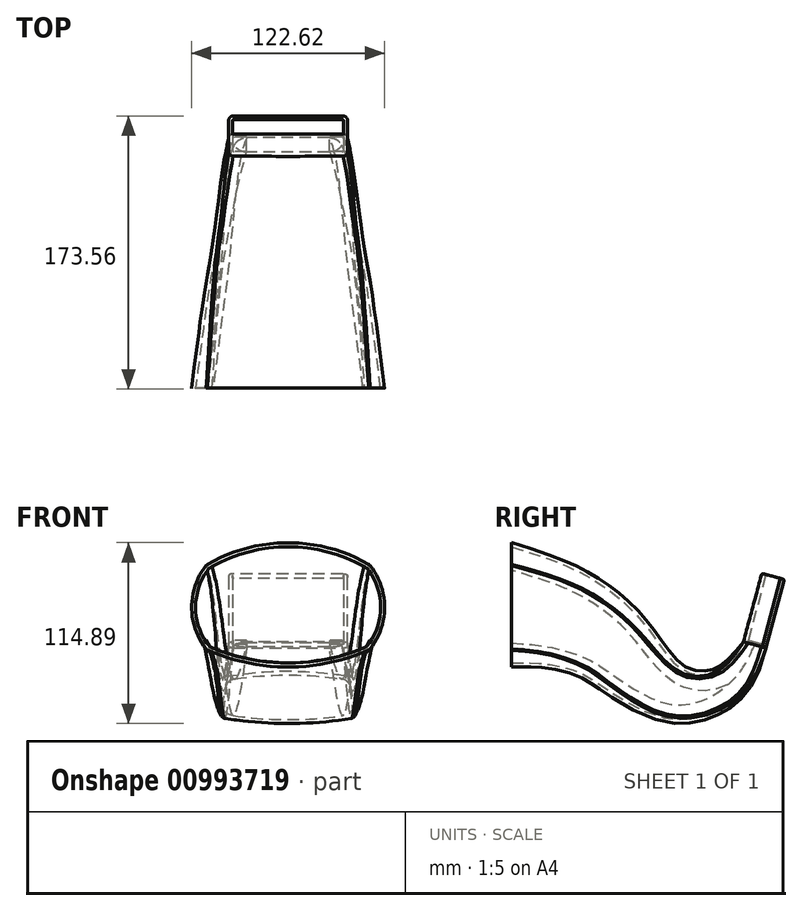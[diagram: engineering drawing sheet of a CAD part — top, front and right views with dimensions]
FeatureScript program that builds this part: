
annotation { "Feature Type Name" : "Feature", "Feature Type Description" : "" }
export const myFeature = defineFeature(function(context is Context, id is Id, definition is map)
    precondition{}
    {
        {
            var Q0;
            Q0=qCreatedBy(makeId("Right.planeOp"),FACE);
            var sketch = newSketch(context, id + "F0", { "sketchPlane" : qUnion([Q0])});
            skLineSegment(sketch, "E0", {"start": v(0, 0) * mm, "end": v(9.05, 33.77) * mm, "construction": true});
            skSolve(sketch);
        }
        {
            var Q0;
            Q0=sQuery(id+"F0.wireOp",EDGE,"E0");
            cPlane(context, id + "F1", {"entities" : qUnion([Q0]), "cplaneType" : CPlaneType.MID_PLANE, "offset" : 25 * mm, "width" : 150 * mm, "height" : 150 * mm});
        }
        {
            var Q0;
            Q0=qCreatedBy(id+"F1.planeOp",FACE);
            var sketch = newSketch(context, id + "F2", { "sketchPlane" : qUnion([Q0])});
            skLineSegment(sketch, "E1.bottom", {"start": v(35.25, 4.75) * mm, "end": v(-35.25, 4.75) * mm});
            skLineSegment(sketch, "E1.top", {"start": v(35.25, -4.75) * mm, "end": v(-35.25, -4.75) * mm});
            skLineSegment(sketch, "E1.left", {"start": v(35.25, 4.75) * mm, "end": v(35.25, -4.75) * mm});
            skLineSegment(sketch, "E1.right", {"start": v(-35.25, 4.75) * mm, "end": v(-35.25, -4.75) * mm});
            skLineSegment(sketch, "E2", {"start": v(35.25, 4.75) * mm, "end": v(-35.25, -4.75) * mm, "construction": true});
            skSolve(sketch);
        }
        {
            var Q0;
            Q0=qCreatedBy(makeId("Right.planeOp"),FACE);
            var sketch = newSketch(context, id + "F3", { "sketchPlane" : qUnion([Q0])});
            skPoint(sketch, "E3.0", {"position": v(4.52, 16.89) * mm});
            skFitSpline(sketch, "E4", {"points": [v(4.52, 16.89) * mm, v(-21.2, -13.25) * mm, v(-50.69, -13.25) * mm, v(-82.93, 11.56) * mm, v(-109.4, 29.2) * mm, v(-150, 40.77) * mm], "startDerivative": vector(-59.2, -227.9) * mm, "endDerivative": vector(-84.83, -3.64) * mm});
            skSolve(sketch);
        }
        {
            var Q0;
            Q0=qCreatedBy(makeId("Front.planeOp"),FACE);
            cPlane(context, id + "F4", {"entities" : qUnion([Q0]), "cplaneType" : CPlaneType.OFFSET, "offset" : 150 * mm, "width" : 150 * mm, "height" : 150 * mm});
        }
        {
            var Q0;
            Q0=qCreatedBy(id+"F4.planeOp",FACE);
            var sketch = newSketch(context, id + "F5", { "sketchPlane" : qUnion([Q0])});
            skLineSegment(sketch, "E5.bottom", {"start": v(-50, 65.77) * mm, "end": v(50, 65.77) * mm, "construction": true});
            skLineSegment(sketch, "E5.top", {"start": v(-50, 15.77) * mm, "end": v(50, 15.77) * mm, "construction": true});
            skLineSegment(sketch, "E5.left", {"start": v(-50, 65.77) * mm, "end": v(-50, 15.77) * mm, "construction": true});
            skLineSegment(sketch, "E5.right", {"start": v(50, 65.77) * mm, "end": v(50, 15.77) * mm, "construction": true});
            skLineSegment(sketch, "E6", {"start": v(-50, 65.77) * mm, "end": v(50, 15.77) * mm, "construction": true});
            skArc(sketch, "E7", {"start": v(50, 65.77) * mm, "mid": v(0, 79.17) * mm, "end": v(-50, 65.77) * mm});
            skArc(sketch, "E8", {"start": v(50, 15.77) * mm, "mid": v(58.78, 40.77) * mm, "end": v(50, 65.77) * mm});
            skArc(sketch, "E9", {"start": v(-50, 65.77) * mm, "mid": v(-58.78, 40.77) * mm, "end": v(-50, 15.77) * mm});
            skArc(sketch, "E10", {"start": v(-50, 15.77) * mm, "mid": v(0, 5.33) * mm, "end": v(50, 15.77) * mm});
            skSolve(sketch);
        }
        {
            var Q0;
            Q0=sQuery(id+"F3.wireOp",EDGE,"E4");
            var Q1;
            Q1=makeQuery(id+"F2.imprint","IMPRINT",FACE,{"disambiguationData":[TD([[makeQuery(id+"F2.imprint","IMPRINT",EDGE,{"derivedFrom":sQuery(id+"F2.wireOp",EDGE,"E1.bottom")}),1.0]])]});
            var Q2;
            Q2=makeQuery(id+"F5.imprint","IMPRINT",FACE,{"disambiguationData":[TD([[makeQuery(id+"F5.imprint","IMPRINT",EDGE,{"derivedFrom":sQuery(id+"F5.wireOp",EDGE,"E7")}),1.0]])]});
            loft(context, id + "F6", {"addSections" : true, "spine" : qUnion([Q0]), "sectionCount" : 5, "sheetProfilesArray" : [{ "sheetProfileEntities" : qUnion([Q1]) }, { "sheetProfileEntities" : qUnion([Q2]) }]});
        }
        {
            var Q0;
            Q0=makeQuery(id+"F6.opLoft","CAP_FACE",FACE,{"disambiguationData":[OSD([makeQuery(id+"F5.imprint","IMPRINT",FACE,{"disambiguationData":[TD([[makeQuery(id+"F5.imprint","IMPRINT",EDGE,{"derivedFrom":sQuery(id+"F5.wireOp",EDGE,"E7")}),1.0]])]})])],"isStart":true});
            var Q1;
            Q1=makeQuery(id+"F6.opLoft","CAP_FACE",FACE,{"disambiguationData":[OSD([makeQuery(id+"F2.imprint","IMPRINT",FACE,{"disambiguationData":[TD([[makeQuery(id+"F2.imprint","IMPRINT",EDGE,{"derivedFrom":sQuery(id+"F2.wireOp",EDGE,"E1.bottom")}),1.0]])]})])],"isStart":true});
            shell(context, id + "F7", {"entities" : qUnion([Q0, Q1]), "thickness" : 2.5 * mm, "oppositeDirection" : true});
        }
        {
            var Q0;
            Q0=makeQuery(id+"F6.opLoft","CAP_FACE",FACE,{"disambiguationData":[OSD([makeQuery(id+"F2.imprint","IMPRINT",FACE,{"disambiguationData":[TD([[makeQuery(id+"F2.imprint","IMPRINT",EDGE,{"derivedFrom":sQuery(id+"F2.wireOp",EDGE,"E1.bottom")}),1.0]])]})])],"isStart":true});
            var sketch = newSketch(context, id + "F8", { "sketchPlane" : qUnion([Q0])});
            skLineSegment(sketch, "E11.bottom", {"start": v(-35.25, -4.75) * mm, "end": v(-26.25, -4.75) * mm});
            skLineSegment(sketch, "E11.top", {"start": v(-35.25, 4.75) * mm, "end": v(-26.25, 4.75) * mm});
            skLineSegment(sketch, "E11.left", {"start": v(-35.25, -4.75) * mm, "end": v(-35.25, 4.75) * mm});
            skLineSegment(sketch, "E11.right", {"start": v(-26.25, -4.75) * mm, "end": v(-26.25, 4.75) * mm});
            skLineSegment(sketch, "E12.bottom", {"start": v(35.25, -4.75) * mm, "end": v(26.25, -4.75) * mm});
            skLineSegment(sketch, "E12.top", {"start": v(35.25, 4.75) * mm, "end": v(26.25, 4.75) * mm});
            skLineSegment(sketch, "E12.left", {"start": v(35.25, -4.75) * mm, "end": v(35.25, 4.75) * mm});
            skLineSegment(sketch, "E12.right", {"start": v(26.25, -4.75) * mm, "end": v(26.25, 4.75) * mm});
            skSolve(sketch);
        }
        {
            var Q0;
            Q0=qSketchRegion(id+"F8",true);
            extrude(context, id + "F9", {"entities" : qUnion([Q0]), "depth" : 1.5 * mm, "offsetDistance" : 25 * mm});
        }
        {
            var Q0;
            Q0=makeQuery(id+"F6.opLoft","CAP_FACE",FACE,{"disambiguationData":[OSD([makeQuery(id+"F2.imprint","IMPRINT",FACE,{"disambiguationData":[TD([[makeQuery(id+"F2.imprint","IMPRINT",EDGE,{"derivedFrom":sQuery(id+"F2.wireOp",EDGE,"E1.bottom")}),1.0]])]})])],"isStart":true});
            extrude(context, id + "F10", {"entities" : qUnion([Q0]), "operationType" : NewBodyOperationType.ADD, "depth" : 45 * mm, "offsetDistance" : 25 * mm});
        }
        {
            var Q0;
            Q0=makeQuery(id+"F7.opShell","OFFSET_EDGE",EDGE,{"disambiguationData":[OSD([sQuery(id+"F2.wireOp",EDGE,"E1.top"),sQuery(id+"F2.wireOp",EDGE,"E1.right"),sQuery(id+"F5.wireOp",EDGE,"E7"),sQuery(id+"F5.wireOp",EDGE,"E9")])]});
            var Q1;
            Q1=makeQuery(id+"F7.opShell","OFFSET_EDGE",EDGE,{"disambiguationData":[OSD([sQuery(id+"F2.wireOp",EDGE,"E1.bottom"),sQuery(id+"F2.wireOp",EDGE,"E1.right"),sQuery(id+"F5.wireOp",EDGE,"E9"),sQuery(id+"F5.wireOp",EDGE,"E10")])]});
            var Q2;
            Q2=makeQuery(id+"F7.opShell","OFFSET_EDGE",EDGE,{"disambiguationData":[OSD([sQuery(id+"F2.wireOp",EDGE,"E1.top"),sQuery(id+"F2.wireOp",EDGE,"E1.left"),sQuery(id+"F5.wireOp",EDGE,"E7"),sQuery(id+"F5.wireOp",EDGE,"E8")])]});
            var Q3;
            Q3=makeQuery(id+"F7.opShell","OFFSET_EDGE",EDGE,{"disambiguationData":[OSD([sQuery(id+"F2.wireOp",EDGE,"E1.bottom"),sQuery(id+"F2.wireOp",EDGE,"E1.left"),sQuery(id+"F5.wireOp",EDGE,"E8"),sQuery(id+"F5.wireOp",EDGE,"E10")])]});
            fillet(context, id + "F11", {"entities" : qUnion([Q0, Q1, Q2, Q3]), "radius" : 9 * mm, "tangentPropagation" : true, "allowEdgeOverflow" : false});
        }
        {
            var Q0;
            {var subQ0=sQuery(id+"F2.wireOp",EDGE,"E1.left");var subQ1=sQuery(id+"F2.wireOp",EDGE,"E1.top");Q0=makeQuery(id+"F10.opExtrude","SWEPT_EDGE",EDGE,{"disambiguationData":[OSD([subQ1,subQ0]),TDD([makeQuery(id+"F6.opLoft","MID_CAP_VERTEX",VERTEX,{"disambiguationData":[OSD([subQ1,subQ0])],"capPos":0.0})])]});}
            var Q1;
            {var subQ0=sQuery(id+"F2.wireOp",EDGE,"E1.right");var subQ1=sQuery(id+"F2.wireOp",EDGE,"E1.top");Q1=makeQuery(id+"F10.opExtrude","SWEPT_EDGE",EDGE,{"disambiguationData":[OSD([subQ1,subQ0]),TDD([makeQuery(id+"F6.opLoft","MID_CAP_VERTEX",VERTEX,{"disambiguationData":[OSD([subQ1,subQ0])],"capPos":0.0})])]});}
            var Q2;
            {var subQ0=sQuery(id+"F2.wireOp",EDGE,"E1.right");var subQ1=sQuery(id+"F2.wireOp",EDGE,"E1.bottom");Q2=makeQuery(id+"F10.opExtrude","SWEPT_EDGE",EDGE,{"disambiguationData":[OSD([subQ1,subQ0]),TDD([makeQuery(id+"F6.opLoft","MID_CAP_VERTEX",VERTEX,{"disambiguationData":[OSD([subQ1,subQ0])],"capPos":0.0})])]});}
            var Q3;
            {var subQ0=sQuery(id+"F2.wireOp",EDGE,"E1.left");var subQ1=sQuery(id+"F2.wireOp",EDGE,"E1.bottom");Q3=makeQuery(id+"F10.opExtrude","SWEPT_EDGE",EDGE,{"disambiguationData":[OSD([subQ1,subQ0]),TDD([makeQuery(id+"F6.opLoft","MID_CAP_VERTEX",VERTEX,{"disambiguationData":[OSD([subQ1,subQ0])],"capPos":0.0})])]});}
            var Q4;
            Q4=makeQuery(id+"F6.opLoft","SWEPT_EDGE",EDGE,{"disambiguationData":[OSD([sQuery(id+"F2.wireOp",EDGE,"E1.top"),sQuery(id+"F2.wireOp",EDGE,"E1.left"),sQuery(id+"F5.wireOp",EDGE,"E7"),sQuery(id+"F5.wireOp",EDGE,"E8")])]});
            var Q5;
            Q5=makeQuery(id+"F6.opLoft","SWEPT_EDGE",EDGE,{"disambiguationData":[OSD([sQuery(id+"F2.wireOp",EDGE,"E1.top"),sQuery(id+"F2.wireOp",EDGE,"E1.right"),sQuery(id+"F5.wireOp",EDGE,"E7"),sQuery(id+"F5.wireOp",EDGE,"E9")])]});
            var Q6;
            Q6=makeQuery(id+"F6.opLoft","SWEPT_EDGE",EDGE,{"disambiguationData":[OSD([sQuery(id+"F2.wireOp",EDGE,"E1.bottom"),sQuery(id+"F2.wireOp",EDGE,"E1.right"),sQuery(id+"F5.wireOp",EDGE,"E9"),sQuery(id+"F5.wireOp",EDGE,"E10")])]});
            var Q7;
            Q7=makeQuery(id+"F6.opLoft","SWEPT_EDGE",EDGE,{"disambiguationData":[OSD([sQuery(id+"F2.wireOp",EDGE,"E1.bottom"),sQuery(id+"F2.wireOp",EDGE,"E1.left"),sQuery(id+"F5.wireOp",EDGE,"E8"),sQuery(id+"F5.wireOp",EDGE,"E10")])]});
            fillet(context, id + "F12", {"entities" : qUnion([Q0, Q1, Q2, Q3, Q4, Q5, Q6, Q7]), "radius" : 3 * mm, "tangentPropagation" : true, "allowEdgeOverflow" : false});
        }
        {
            var Q0;
            {var subQ0=sQuery(id+"F2.wireOp",EDGE,"E1.right");var subQ1=sQuery(id+"F2.wireOp",EDGE,"E1.top");Q0=makeQuery(id+"F10.opExtrude","SWEPT_EDGE",EDGE,{"disambiguationData":[OSD([subQ1,subQ0]),TDD([makeQuery(id+"F7.opShell","OFFSET_VERTEX",VERTEX,{"disambiguationData":[OSD([subQ1,subQ0])]})])]});}
            var Q1;
            {var subQ0=sQuery(id+"F2.wireOp",EDGE,"E1.right");var subQ1=sQuery(id+"F2.wireOp",EDGE,"E1.bottom");Q1=makeQuery(id+"F10.opExtrude","SWEPT_EDGE",EDGE,{"disambiguationData":[OSD([subQ1,subQ0]),TDD([makeQuery(id+"F7.opShell","OFFSET_VERTEX",VERTEX,{"disambiguationData":[OSD([subQ1,subQ0])]})])]});}
            var Q2;
            {var subQ0=sQuery(id+"F2.wireOp",EDGE,"E1.left");var subQ1=sQuery(id+"F2.wireOp",EDGE,"E1.bottom");Q2=makeQuery(id+"F10.opExtrude","SWEPT_EDGE",EDGE,{"disambiguationData":[OSD([subQ1,subQ0]),TDD([makeQuery(id+"F7.opShell","OFFSET_VERTEX",VERTEX,{"disambiguationData":[OSD([subQ1,subQ0])]})])]});}
            var Q3;
            {var subQ0=sQuery(id+"F2.wireOp",EDGE,"E1.left");var subQ1=sQuery(id+"F2.wireOp",EDGE,"E1.top");Q3=makeQuery(id+"F10.opExtrude","SWEPT_EDGE",EDGE,{"disambiguationData":[OSD([subQ1,subQ0]),TDD([makeQuery(id+"F7.opShell","OFFSET_VERTEX",VERTEX,{"disambiguationData":[OSD([subQ1,subQ0])]})])]});}
            var Q4;
            {var subQ0=sQuery(id+"F2.wireOp",EDGE,"E1.right");var subQ1=sQuery(id+"F2.wireOp",EDGE,"E1.left");var subQ2=sQuery(id+"F2.wireOp",EDGE,"E1.top");Q4=makeQuery(id+"F10.opExtrude","CAP_EDGE",EDGE,{"disambiguationData":[OSD([subQ2,subQ1,subQ0]),TDD([makeQuery(id+"F7.opShell","OFFSET_EDGE",EDGE,{"disambiguationData":[OSD([subQ2,subQ1,subQ0])]})])],"isStart":false});}
            var Q5;
            {var subQ0=sQuery(id+"F2.wireOp",EDGE,"E1.right");var subQ1=sQuery(id+"F2.wireOp",EDGE,"E1.left");var subQ2=sQuery(id+"F2.wireOp",EDGE,"E1.bottom");Q5=makeQuery(id+"F10.opExtrude","CAP_EDGE",EDGE,{"disambiguationData":[OSD([subQ2,subQ1,subQ0]),TDD([makeQuery(id+"F6.opLoft","MID_CAP_EDGE",EDGE,{"disambiguationData":[OSD([subQ2,subQ1,subQ0])],"capPos":0.0})])],"isStart":false});}
            fillet(context, id + "F13", {"entities" : qUnion([Q0, Q1, Q2, Q3, Q4, Q5]), "radius" : 1 * mm, "tangentPropagation" : true, "allowEdgeOverflow" : false});
        }
    });
